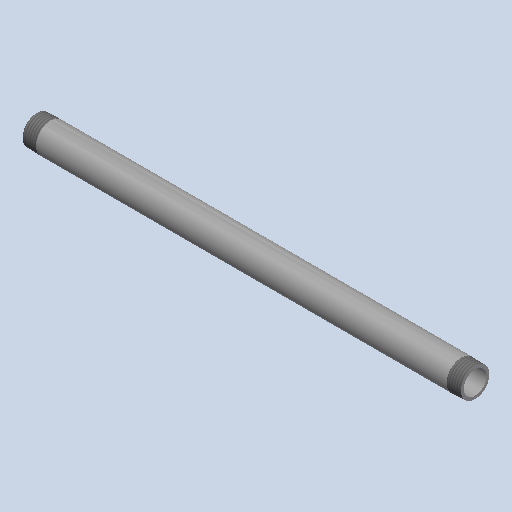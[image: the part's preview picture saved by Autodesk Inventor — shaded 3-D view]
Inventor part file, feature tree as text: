
AUTODESK INVENTOR PART (.ipt)
format: ipt  version: 2025 (Build 290162000, 162)  size: 164,352 bytes
history: native  units: mm (DEFAULTED — no unit token found)
features: other x8, revolve x1
ambient origin geometry x8: Origin, YZ Plane, XZ Plane, XY Plane, X Axis, Y Axis, Z Axis, Center Point
bodies: Solid1 (feature_tree)
feature tree (9):
  revolve  "Revolution1"  [1 undecoded]
  other  "Work Axis1"
  other  "Work Point5"
  other  "Work Axis2"
  other  "Work Point6"
  other  "Work Axis3"
  other  "Work Axis4"
  other  "Work Point7"
  other  "Work Point8"
note: 1 required parameter value undecoded (feature->parameter linkage not recoverable at this tier; creation-order binding heuristic only, values carry confidence <= 0.55)
